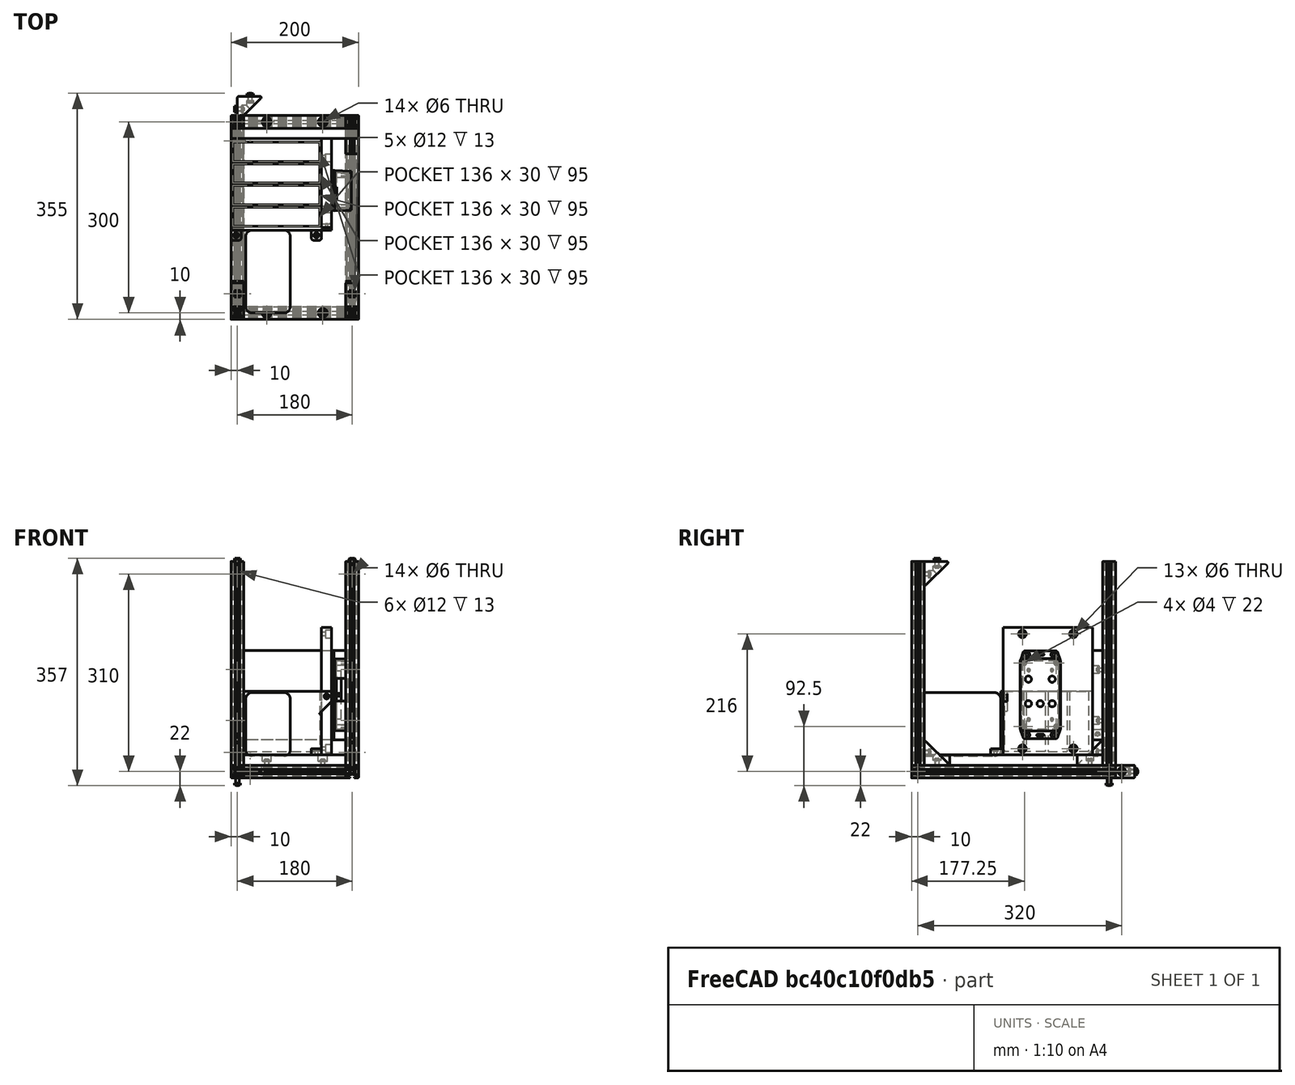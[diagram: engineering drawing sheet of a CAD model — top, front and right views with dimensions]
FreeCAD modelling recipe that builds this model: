
FCSTD DOCUMENT  (FreeCAD 0.17R9796 (Git))
Label: UPKframeNG2d
License: All rights reserved
LicenseURL: http://en.wikipedia.org/wiki/All_rights_reserved
objects: Part::Feature×60, Part::FeaturePython×24, Part::Compound×12, App::FeaturePython×8, App::Part×6, Part::Cylinder×5, Part::Box×4, Part::Cut×4, PartDesign::Body×2, PartDesign::Pocket×1, Part::Fillet×1, Part::MultiFuse×1
note: 115 computed .brp shape members not serialized (recipe doc carries the construction recipe); baked Part::Feature solids carry a one-line shape summary decoded from their .brp

FEATURE [Part::Feature] Pocket003001  label="tslot32con"
  Placement = pos=(0,10,10) rot=(1,0,0;1.5708rad)
  shape: bbox 20 x 320 x 20 mm, 150 faces (baked)
FEATURE [Part::Feature] Pocket003002  label="tslot16"
  Placement = pos=(10,0,10) rot=(0,1,0;1.5708rad)
  shape: bbox 160 x 20 x 20 mm, 94 faces (baked)
FEATURE [Part::Feature] Pocket003006  label="tslot16_001"
  Placement = pos=(10,-300,10) rot=(0,1,0;1.5708rad)
  shape: bbox 160 x 20 x 20 mm, 94 faces (baked)
FEATURE [Part::Feature] Pocket003007  label="tslot32con_001"
  Placement = pos=(180,-310,10) rot=(0,0.707107,0.707107;3.14159rad)
  shape: bbox 20 x 320 x 20 mm, 150 faces (baked)
FEATURE [Part::FeaturePython] Screw  label="M6x25-Screw"  # Fasteners workbench fastener (typed FeaturePython)
  Placement = pos=(-4,0,10) rot=(0,-1,0;1.5708rad)
  diameter = 7
  invert = false
  length = 6
  matchOuter = false
  offset = 0
  thread = false
  type = 15
FEATURE [Part::FeaturePython] Screw001  label="M6x25-Screw004"  # Fasteners workbench fastener (typed FeaturePython)
  Placement = pos=(-4,-300,10) rot=(0,-1,0;1.5708rad)
  diameter = 7
  invert = false
  length = 6
  matchOuter = false
  offset = 0
  thread = false
  type = 15
FEATURE [Part::FeaturePython] Screw002  label="M6x25-Screw005"  # Fasteners workbench fastener (typed FeaturePython)
  Placement = pos=(184,0,10) rot=(0,1,0;1.5708rad)
  diameter = 7
  invert = false
  length = 6
  matchOuter = false
  offset = 0
  thread = false
  type = 15
FEATURE [Part::FeaturePython] Screw004  label="M6x25-Screw006"  # Fasteners workbench fastener (typed FeaturePython)
  Placement = pos=(184,-300,10) rot=(0,1,0;1.5708rad)
  diameter = 7
  invert = false
  length = 6
  matchOuter = false
  offset = 0
  thread = false
  type = 15
FEATURE [App::Part] Part  label="lower_frame"
  Group = -> [Pocket003001,Pocket003002,Pocket003006,Pocket003007,Screw,Screw001,Screw002,Screw004]
  License = CC BY 3.0
  LicenseURL = http://creativecommons.org/licenses/by/3.0/
  Origin = -> PartOrigin
FEATURE [Part::Feature] Pocket003008  label="tslot32con001"
  Placement = pos=(0,10,10) rot=(1,0,0;1.5708rad)
  shape: bbox 20 x 320 x 20 mm, 150 faces (baked)
FEATURE [Part::Feature] Pocket003009  label="tslot041"
  Placement = pos=(10,0,10) rot=(0,1,0;1.5708rad)
  shape: bbox 160 x 20 x 20 mm, 94 faces (baked)
FEATURE [Part::Feature] Pocket003010  label="tslot16_002"
  Placement = pos=(10,-300,10) rot=(0,1,0;1.5708rad)
  shape: bbox 160 x 20 x 20 mm, 94 faces (baked)
FEATURE [Part::Feature] Pocket003011  label="tslot32con_002"
  Placement = pos=(180,-310,10) rot=(0,0.707107,0.707107;3.14159rad)
  shape: bbox 20 x 320 x 20 mm, 150 faces (baked)
FEATURE [Part::FeaturePython] Screw005  label="M6x25-Screw007"  # Fasteners workbench fastener (typed FeaturePython)
  Placement = pos=(-4,0,10) rot=(0,-1,0;1.5708rad)
  diameter = 7
  invert = false
  length = 6
  matchOuter = false
  offset = 0
  thread = false
  type = 15
FEATURE [Part::FeaturePython] Screw006  label="M6x25-Screw008"  # Fasteners workbench fastener (typed FeaturePython)
  Placement = pos=(-4,-300,10) rot=(0,-1,0;1.5708rad)
  diameter = 7
  invert = false
  length = 6
  matchOuter = false
  offset = 0
  thread = false
  type = 15
FEATURE [Part::FeaturePython] Screw007  label="M6x25-Screw009"  # Fasteners workbench fastener (typed FeaturePython)
  Placement = pos=(184,0,10) rot=(0,1,0;1.5708rad)
  diameter = 7
  invert = false
  length = 6
  matchOuter = false
  offset = 0
  thread = false
  type = 15
FEATURE [Part::FeaturePython] Screw008  label="M6x25-Screw010"  # Fasteners workbench fastener (typed FeaturePython)
  Placement = pos=(184,-300,10) rot=(0,1,0;1.5708rad)
  diameter = 7
  invert = false
  length = 6
  matchOuter = false
  offset = 0
  thread = false
  type = 15
FEATURE [App::Part] Part001  label="upper_frame"
  Group = -> [Pocket003008,Pocket003009,Pocket003010,Pocket003011,Screw005,Screw006,Screw007,Screw008]
  License = CC BY 3.0
  LicenseURL = http://creativecommons.org/licenses/by/3.0/
  Origin = -> PartOrigin001
  Placement = pos=(0,0,340) rot=(0,0,1;0rad)
FEATURE [Part::Feature] Fillet004001  label="Fillet005"
  shape: bbox 37.5 x 37.5 x 20 mm, 26 faces (baked)
FEATURE [Part::FeaturePython] Screw009  label="M6x12-Screw"  # Fasteners workbench fastener (typed FeaturePython)
  Placement = pos=(7,20,10) rot=(0,1,0;1.5708rad)
  diameter = 4
  invert = false
  length = 1
  matchOuter = false
  offset = 0
  thread = false
  type = 20
FEATURE [Part::Feature] Body001  label="m6nutplate"
  Placement = pos=(-1.5,15,5) rot=(0,-1,0;1.5708rad)
  shape: bbox 3 x 10 x 10 mm, 9 faces (baked)
FEATURE [App::Part] Part002  label="cornerstonescrewnut"
  License = CC BY 3.0
  LicenseURL = http://creativecommons.org/licenses/by/3.0/
  Origin = -> PartOrigin002
  Placement = pos=(10,-50,20) rot=(0,-1,0;1.5708rad)
FEATURE [Part::FeaturePython] Screw010  label="M6x12-Screw001"  # Fasteners workbench fastener (typed FeaturePython)
  Placement = pos=(20,33,10) rot=(1,0,0;1.5708rad)
  diameter = 4
  invert = false
  length = 1
  matchOuter = false
  offset = 0
  thread = false
  type = 20
FEATURE [Part::Feature] Body002  label="m6nutplate001"
  Placement = pos=(15,41.5,5) rot=(0.57735,0.57735,0.57735;4.18879rad)
  shape: bbox 10 x 3 x 10 mm, 9 faces (baked)
FEATURE [Part::Feature] Fillet004002  label="Fillet006"
  shape: bbox 37.5 x 37.5 x 20 mm, 26 faces (baked)
FEATURE [Part::FeaturePython] Screw011  label="M6x12-Screw002"  # Fasteners workbench fastener (typed FeaturePython)
  Placement = pos=(7,20,10) rot=(0,1,0;1.5708rad)
  diameter = 4
  invert = false
  length = 1
  matchOuter = false
  offset = 0
  thread = false
  type = 20
FEATURE [Part::Feature] Body003  label="m6nutplate002"
  Placement = pos=(-1.5,15,5) rot=(0,-1,0;1.5708rad)
  shape: bbox 3 x 10 x 10 mm, 9 faces (baked)
FEATURE [Part::FeaturePython] Screw012  label="M6x12-Screw003"  # Fasteners workbench fastener (typed FeaturePython)
  Placement = pos=(20,33,10) rot=(1,0,0;1.5708rad)
  diameter = 4
  invert = false
  length = 1
  matchOuter = false
  offset = 0
  thread = false
  type = 20
FEATURE [Part::Feature] Body004  label="m6nutplate003"
  Placement = pos=(15,41.5,5) rot=(0.57735,0.57735,0.57735;4.18879rad)
  shape: bbox 10 x 3 x 10 mm, 9 faces (baked)
FEATURE [App::Part] Part003  label="cornerstonescrewnut001"
  Group = -> [Body003,Screw011,Fillet004002,Screw012,Body004,PartOrigin002,Body001,Screw009,Fillet004001,Screw010,Body002,Part002]
  License = CC BY 3.0
  LicenseURL = http://creativecommons.org/licenses/by/3.0/
  Origin = -> PartOrigin003
  Placement = pos=(190,-50,20) rot=(0,-1,0;1.5708rad)
FEATURE [Part::Feature] Fillet004003  label="Fillet007"
  shape: bbox 37.5 x 37.5 x 20 mm, 26 faces (baked)
FEATURE [Part::FeaturePython] Screw013  label="M6x12-Screw004"  # Fasteners workbench fastener (typed FeaturePython)
  Placement = pos=(7,20,10) rot=(0,1,0;1.5708rad)
  diameter = 4
  invert = false
  length = 1
  matchOuter = false
  offset = 0
  thread = false
  type = 20
FEATURE [Part::Feature] Body005  label="m6nutplate004"
  Placement = pos=(-1.5,15,5) rot=(0,-1,0;1.5708rad)
  shape: bbox 3 x 10 x 10 mm, 9 faces (baked)
FEATURE [Part::FeaturePython] Screw014  label="M6x12-Screw005"  # Fasteners workbench fastener (typed FeaturePython)
  Placement = pos=(20,33,10) rot=(1,0,0;1.5708rad)
  diameter = 4
  invert = false
  length = 1
  matchOuter = false
  offset = 0
  thread = false
  type = 20
FEATURE [Part::Feature] Body006  label="m6nutplate005"
  Placement = pos=(15,41.5,5) rot=(0.57735,0.57735,0.57735;4.18879rad)
  shape: bbox 10 x 3 x 10 mm, 9 faces (baked)
FEATURE [App::Part] Part004  label="cornerstonescrewnut002"
  Group = -> [Body005,Screw013,Fillet004003,Screw014,Body006]
  License = CC BY 3.0
  LicenseURL = http://creativecommons.org/licenses/by/3.0/
  Origin = -> PartOrigin004
  Placement = pos=(-10,-50,340) rot=(0,1,0;1.5708rad)
FEATURE [Part::Feature] Fillet004004  label="Fillet008"
  shape: bbox 37.5 x 37.5 x 20 mm, 26 faces (baked)
FEATURE [Part::FeaturePython] Screw015  label="M6x12-Screw006"  # Fasteners workbench fastener (typed FeaturePython)
  Placement = pos=(7,20,10) rot=(0,1,0;1.5708rad)
  diameter = 4
  invert = false
  length = 1
  matchOuter = false
  offset = 0
  thread = false
  type = 20
FEATURE [Part::Feature] Body007  label="m6nutplate006"
  Placement = pos=(-1.5,15,5) rot=(0,-1,0;1.5708rad)
  shape: bbox 3 x 10 x 10 mm, 9 faces (baked)
FEATURE [Part::FeaturePython] Screw016  label="M6x12-Screw007"  # Fasteners workbench fastener (typed FeaturePython)
  Placement = pos=(20,33,10) rot=(1,0,0;1.5708rad)
  diameter = 4
  invert = false
  length = 1
  matchOuter = false
  offset = 0
  thread = false
  type = 20
FEATURE [Part::Feature] Body008  label="m6nutplate007"
  Placement = pos=(15,41.5,5) rot=(0.57735,0.57735,0.57735;4.18879rad)
  shape: bbox 10 x 3 x 10 mm, 9 faces (baked)
FEATURE [App::Part] Part005  label="cornerstonescrewnut003"
  Group = -> [Body007,Screw015,Fillet004004,Screw016,Body008]
  License = CC BY 3.0
  LicenseURL = http://creativecommons.org/licenses/by/3.0/
  Origin = -> PartOrigin005
  Placement = pos=(170,-50,340) rot=(0,1,0;1.5708rad)
FEATURE [Part::Feature] Body009001  label="m6nutplate010"
  Placement = pos=(-1.5,15,5) rot=(0,-1,0;1.5708rad)
  shape: bbox 3 x 10 x 10 mm, 9 faces (baked)
FEATURE [Part::Feature] Body010001  label="m6nutplate011"
  Placement = pos=(15,41.5,5) rot=(0.57735,0.57735,0.57735;4.18879rad)
  shape: bbox 10 x 3 x 10 mm, 9 faces (baked)
FEATURE [Part::Feature] Screw018001  label="M6x12-Screw010"
  Placement = pos=(20,33,10) rot=(1,0,0;1.5708rad)
  shape: bbox 10.5 x 15.3 x 10.5 mm, 15 faces (baked)
FEATURE [Part::Feature] Screw017001  label="M6x12-Screw011"
  Placement = pos=(7,20,10) rot=(0,1,0;1.5708rad)
  shape: bbox 15.3 x 10.5 x 10.5 mm, 15 faces (baked)
FEATURE [Part::Feature] Fillet004005001  label="Fillet010"
  shape: bbox 37.5 x 37.5 x 20 mm, 26 faces (baked)
FEATURE [Part::Compound] Compound
  Links = -> [Body009001,Fillet004005001,Screw017001,Body010001,Screw018001]
  Placement = pos=(10,-250,340) rot=(0.707107,0,-0.707107;3.14159rad)
FEATURE [Part::Feature] Body010002  label="m6nutplate012"
  Placement = pos=(-1.5,15,5) rot=(0,-1,0;1.5708rad)
  shape: bbox 3 x 10 x 10 mm, 9 faces (baked)
FEATURE [Part::Feature] Body010003  label="m6nutplate013"
  Placement = pos=(15,41.5,5) rot=(0.57735,0.57735,0.57735;4.18879rad)
  shape: bbox 10 x 3 x 10 mm, 9 faces (baked)
FEATURE [Part::Feature] Screw018002  label="M6x12-Screw012"
  Placement = pos=(20,33,10) rot=(1,0,0;1.5708rad)
  shape: bbox 10.5 x 15.3 x 10.5 mm, 15 faces (baked)
FEATURE [Part::Feature] Screw018003  label="M6x12-Screw013"
  Placement = pos=(7,20,10) rot=(0,1,0;1.5708rad)
  shape: bbox 15.3 x 10.5 x 10.5 mm, 15 faces (baked)
FEATURE [Part::Feature] Fillet004005002  label="Fillet011"
  shape: bbox 37.5 x 37.5 x 20 mm, 26 faces (baked)
FEATURE [Part::Compound] Compound001
  Links = -> [Body010002,Fillet004005002,Screw018003,Body010003,Screw018002]
  Placement = pos=(190,-250,340) rot=(0.707107,0,-0.707107;3.14159rad)
FEATURE [Part::Feature] Body010004  label="m6nutplate014"
  Placement = pos=(-1.5,15,5) rot=(0,-1,0;1.5708rad)
  shape: bbox 3 x 10 x 10 mm, 9 faces (baked)
FEATURE [Part::Feature] Body010005  label="m6nutplate015"
  Placement = pos=(15,41.5,5) rot=(0.57735,0.57735,0.57735;4.18879rad)
  shape: bbox 10 x 3 x 10 mm, 9 faces (baked)
FEATURE [Part::Feature] Screw018004  label="M6x12-Screw014"
  Placement = pos=(20,33,10) rot=(1,0,0;1.5708rad)
  shape: bbox 10.5 x 15.3 x 10.5 mm, 15 faces (baked)
FEATURE [Part::Feature] Screw018005  label="M6x12-Screw015"
  Placement = pos=(7,20,10) rot=(0,1,0;1.5708rad)
  shape: bbox 15.3 x 10.5 x 10.5 mm, 15 faces (baked)
FEATURE [Part::Feature] Fillet004005003  label="Fillet012"
  shape: bbox 37.5 x 37.5 x 20 mm, 26 faces (baked)
FEATURE [Part::Compound] Compound002
  Links = -> [Body010004,Fillet004005003,Screw018005,Body010005,Screw018004]
  Placement = pos=(10,-290,60) rot=(0.57735,0.57735,-0.57735;4.18879rad)
FEATURE [Part::Feature] Body010006  label="m6nutplate016"
  Placement = pos=(-1.5,15,5) rot=(0,-1,0;1.5708rad)
  shape: bbox 3 x 10 x 10 mm, 9 faces (baked)
FEATURE [Part::Feature] Body010007  label="m6nutplate017"
  Placement = pos=(15,41.5,5) rot=(0.57735,0.57735,0.57735;4.18879rad)
  shape: bbox 10 x 3 x 10 mm, 9 faces (baked)
FEATURE [Part::Feature] Screw018006  label="M6x12-Screw016"
  Placement = pos=(20,33,10) rot=(1,0,0;1.5708rad)
  shape: bbox 10.5 x 15.3 x 10.5 mm, 15 faces (baked)
FEATURE [Part::Feature] Screw018007  label="M6x12-Screw017"
  Placement = pos=(7,20,10) rot=(0,1,0;1.5708rad)
  shape: bbox 15.3 x 10.5 x 10.5 mm, 15 faces (baked)
FEATURE [Part::Feature] Fillet004005004  label="Fillet013"
  shape: bbox 37.5 x 37.5 x 20 mm, 26 faces (baked)
FEATURE [Part::Compound] Compound003
  Links = -> [Body010006,Fillet004005004,Screw018007,Body010007,Screw018006]
  Placement = pos=(190,-290,60) rot=(0.57735,0.57735,-0.57735;4.18879rad)
FEATURE [Part::Feature] Pocket001001  label="tslot32"
  Placement = pos=(0,0,20) rot=(0,0,1;0rad)
  shape: bbox 20 x 20 x 320 mm, 94 faces (baked)
FEATURE [Part::Feature] Body010008  label="m6nutplate018"
  Placement = pos=(-1.5,15,5) rot=(0,-1,0;1.5708rad)
  shape: bbox 3 x 10 x 10 mm, 9 faces (baked)
FEATURE [Part::Feature] Body010009  label="m6nutplate019"
  Placement = pos=(15,41.5,5) rot=(0.57735,0.57735,0.57735;4.18879rad)
  shape: bbox 10 x 3 x 10 mm, 9 faces (baked)
FEATURE [Part::Feature] Screw018008  label="M6x12-Screw018"
  Placement = pos=(20,33,10) rot=(1,0,0;1.5708rad)
  shape: bbox 10.5 x 15.3 x 10.5 mm, 15 faces (baked)
FEATURE [Part::Feature] Screw018009  label="M6x12-Screw019"
  Placement = pos=(7,20,10) rot=(0,1,0;1.5708rad)
  shape: bbox 15.3 x 10.5 x 10.5 mm, 15 faces (baked)
FEATURE [Part::Feature] Fillet004005005  label="Fillet014"
  shape: bbox 37.5 x 37.5 x 20 mm, 26 faces (baked)
FEATURE [Part::Compound] Compound004
  Links = -> [Body010008,Fillet004005005,Screw018009,Body010009,Screw018008]
  Placement = pos=(-10,-10,60) rot=(0.57735,-0.57735,0.57735;4.18879rad)
FEATURE [Part::Feature] Pocket003012  label="tslot32_001"
  Placement = pos=(0,-300,20) rot=(0,0,1;0rad)
  shape: bbox 20 x 20 x 320 mm, 94 faces (baked)
FEATURE [Part::Feature] Pocket003013  label="tslot32_002"
  Placement = pos=(180,0,20) rot=(0,0,1;0rad)
  shape: bbox 20 x 20 x 320 mm, 94 faces (baked)
FEATURE [Part::Feature] Pocket003014  label="tslot32_003"
  Placement = pos=(180,-300,20) rot=(0,0,1;0rad)
  shape: bbox 20 x 20 x 320 mm, 94 faces (baked)
FEATURE [PartDesign::Body] Body010027
FEATURE [Part::FeaturePython] Screw018021  label="M6x12-Screw032"  # Fasteners workbench fastener (typed FeaturePython)
  diameter = 4
  invert = false
  length = 1
  matchOuter = false
  offset = 0
  thread = false
  type = 20
FEATURE [Part::Feature] Body010028  label="m6nutplate032"
  Placement = pos=(5,-5,-8.39) rot=(0,1,0;3.14159rad)
  shape: bbox 10 x 10 x 3 mm, 9 faces (baked)
FEATURE [App::FeaturePython] circularEdgeConstraint009  # a2plus constraint (typed FeaturePython)
  Object1 = Screw
  Object2 = Body001
  SubElement1 = Edge7
  SubElement2 = Edge20
  Type = circularEdge
  directionConstraint = 1
  lockRotation = false
  offset = 0
FEATURE [Part::Compound] Compound017  label="nutplate12screw008"
  Links = -> [Screw018021,circularEdgeConstraint009,Body010028]
  Placement = pos=(10,30,6) rot=(0,0,1;0rad)
FEATURE [Part::FeaturePython] Screw018022  label="M6x12-Screw033"  # Fasteners workbench fastener (typed FeaturePython)
  diameter = 4
  invert = false
  length = 1
  matchOuter = false
  offset = 0
  thread = false
  type = 20
FEATURE [Part::Feature] Body010029  label="m6nutplate033"
  Placement = pos=(5,-5,-8.39) rot=(0,1,0;3.14159rad)
  shape: bbox 10 x 10 x 3 mm, 9 faces (baked)
FEATURE [App::FeaturePython] circularEdgeConstraint010  # a2plus constraint (typed FeaturePython)
  Object1 = Screw
  Object2 = Body001
  SubElement1 = Edge7
  SubElement2 = Edge20
  Type = circularEdge
  directionConstraint = 1
  lockRotation = false
  offset = 0
FEATURE [Part::Compound] Compound018  label="nutplate12screw009"
  Links = -> [Screw018022,circularEdgeConstraint010,Body010029]
  Placement = pos=(10,110,6) rot=(0,0,1;0rad)
FEATURE [Part::FeaturePython] Screw018023  label="M6x12-Screw034"  # Fasteners workbench fastener (typed FeaturePython)
  diameter = 4
  invert = false
  length = 1
  matchOuter = false
  offset = 0
  thread = false
  type = 20
FEATURE [Part::Feature] Body010030  label="m6nutplate034"
  Placement = pos=(5,-5,-8.39) rot=(0,1,0;3.14159rad)
  shape: bbox 10 x 10 x 3 mm, 9 faces (baked)
FEATURE [App::FeaturePython] circularEdgeConstraint011  # a2plus constraint (typed FeaturePython)
  Object1 = Screw
  Object2 = Body001
  SubElement1 = Edge7
  SubElement2 = Edge20
  Type = circularEdge
  directionConstraint = 1
  lockRotation = false
  offset = 0
FEATURE [Part::Compound] Compound019  label="nutplate12screw010"
  Links = -> [Screw018023,circularEdgeConstraint011,Body010030]
  Placement = pos=(190,110,6) rot=(0,0,1;0rad)
FEATURE [Part::FeaturePython] Screw018024  label="M6x12-Screw035"  # Fasteners workbench fastener (typed FeaturePython)
  diameter = 4
  invert = false
  length = 1
  matchOuter = false
  offset = 0
  thread = false
  type = 20
FEATURE [Part::Feature] Body010031  label="m6nutplate035"
  Placement = pos=(5,-5,-8.39) rot=(0,1,0;3.14159rad)
  shape: bbox 10 x 10 x 3 mm, 9 faces (baked)
FEATURE [App::FeaturePython] circularEdgeConstraint012  # a2plus constraint (typed FeaturePython)
  Object1 = Screw
  Object2 = Body001
  SubElement1 = Edge7
  SubElement2 = Edge20
  Type = circularEdge
  directionConstraint = 1
  lockRotation = false
  offset = 0
FEATURE [Part::Compound] Compound020  label="nutplate12screw011"
  Links = -> [Screw018024,circularEdgeConstraint012,Body010031]
  Placement = pos=(190,30,6) rot=(0,0,1;0rad)
FEATURE [Part::Compound] Compound021  label="front_plate"
  Links = -> [Body010027,Compound020,Compound019,Compound017,Compound018]
  Placement = pos=(-10,-10,60) rot=(1,0,0;1.5708rad)
FEATURE [Part::Compound] Compound016  label="bottom_plate"
  Placement = pos=(190,-310,20) rot=(0,0,1;1.5708rad)
FEATURE [PartDesign::Pocket] Pocket003019
  Length = 10
  Placement = pos=(130,-166,235) rot=(0,1,0;1.5708rad)
  Type = 0
FEATURE [Part::Box] Box003  label="MPPT"
  AttacherType = Attacher::AttachEngine3D
  Height = 100
  Length = 130
  Placement = pos=(290,128,10) rot=(0,0,1;0rad)
  Width = 70
FEATURE [Part::Fillet] Fillet007  label="MPPT               "
  Base = -> Box003
  Edges = 12 edges r=10: [Edge1,Edge2,Edge3,Edge4,Edge5,Edge6,Edge7,Edge8,Edge9,Edge10,Edge11,Edge12]
  Placement = pos=(211,-590,24) rot=(0,0,1;1.5708rad)
FEATURE [Part::Feature] Part__Feature1213  label="1591XXBF LID"
  Placement = pos=(153,-86,180) rot=(-0.57735,0.57735,0.57735;4.18879rad)
  shape: bbox 12.61 x 63.32 x 138 mm, 220 faces (baked)
FEATURE [Part::Feature] Part__Feature1212  label="1591XXB BOX"
  Placement = pos=(0,0,0) rot=(0,0.707107,0.707107;3.14159rad)
  shape: bbox 113.8 x 28.25 x 63.32 mm, 133 faces (baked)
FEATURE [Part::Cylinder] Cylinder  label="Zylinder"
  Angle = 360
  AttacherType = Attacher::AttachEngine3D
  Height = 60
  Placement = pos=(-14,48,18.6) rot=(1,0,0;1.5708rad)
  Radius = 5
FEATURE [Part::Cylinder] Cylinder001  label="Zylinder001"
  Angle = 360
  AttacherType = Attacher::AttachEngine3D
  Height = 60
  Placement = pos=(-14,48,0) rot=(1,0,0;1.5708rad)
  Radius = 5
FEATURE [Part::Cylinder] Cylinder002  label="Zylinder002"
  Angle = 360
  AttacherType = Attacher::AttachEngine3D
  Height = 60
  Placement = pos=(-14,48,-18.66) rot=(1,0,0;1.5708rad)
  Radius = 5
FEATURE [Part::Cylinder] Cylinder003  label="Zylinder003"
  Angle = 360
  AttacherType = Attacher::AttachEngine3D
  Height = 60
  Placement = pos=(24.49,48,18.6) rot=(1,0,0;1.5708rad)
  Radius = 5
FEATURE [Part::Cylinder] Cylinder004  label="Zylinder004"
  Angle = 360
  AttacherType = Attacher::AttachEngine3D
  Height = 60
  Placement = pos=(24.49,48,-18.66) rot=(1,0,0;1.5708rad)
  Radius = 5
FEATURE [Part::MultiFuse] Fusion
  Shapes = -> [Cylinder,Cylinder004,Cylinder003,Cylinder002,Cylinder001]
FEATURE [Part::Cut] Cut
  Base = -> Part__Feature1212
  Tool = -> Fusion
FEATURE [Part::Box] Box002  label="Würfel002"
  AttacherType = Attacher::AttachEngine3D
  Height = 10
  Length = 76
  Placement = pos=(-38,16,-36) rot=(0,0,1;0rad)
  Width = 12.6
FEATURE [Part::Cut] Cut001
  Base = -> Cut
  Tool = -> Box002
FEATURE [Part::Box] Box004  label="Würfel003"
  AttacherType = Attacher::AttachEngine3D
  Height = 10
  Length = 36
  Placement = pos=(-10,9,24) rot=(0,0,1;0rad)
  Width = 20
FEATURE [Part::Cut] Cut002
  Base = -> Cut001
  Tool = -> Box004
FEATURE [Part::Box] Box  label="Würfel"
  AttacherType = Attacher::AttachEngine3D
  Height = 20
  Length = 10
  Placement = pos=(49,23,-6) rot=(0,0,1;0rad)
  Width = 6
FEATURE [Part::Cut] Cut003  label="bms-cover"
  Base = -> Cut002
  Placement = pos=(179,-108,130.5) rot=(0.57735,-0.57735,0.57735;2.0944rad)
  Tool = -> Box
FEATURE [PartDesign::Body] Body010032
FEATURE [Part::FeaturePython] Screw018025  label="M6x12-Screw036"  # Fasteners workbench fastener (typed FeaturePython)
  diameter = 4
  invert = false
  length = 1
  matchOuter = false
  offset = 0
  thread = false
  type = 20
FEATURE [App::FeaturePython] circularEdgeConstraint013  # a2plus constraint (typed FeaturePython)
  Object1 = Screw
  Object2 = Body001
  SubElement1 = Edge7
  SubElement2 = Edge20
  Type = circularEdge
  directionConstraint = 1
  lockRotation = false
  offset = 0
FEATURE [Part::FeaturePython] Screw018026  label="M6x12-Screw037"  # Fasteners workbench fastener (typed FeaturePython)
  diameter = 4
  invert = false
  length = 1
  matchOuter = false
  offset = 0
  thread = false
  type = 20
FEATURE [Part::Feature] Body010034  label="m6nutplate037"
  Placement = pos=(5,-5,-8.39) rot=(0,1,0;3.14159rad)
  shape: bbox 10 x 10 x 3 mm, 9 faces (baked)
FEATURE [App::FeaturePython] circularEdgeConstraint014  # a2plus constraint (typed FeaturePython)
  Object1 = Screw
  Object2 = Body001
  SubElement1 = Edge7
  SubElement2 = Edge20
  Type = circularEdge
  directionConstraint = 1
  lockRotation = false
  offset = 0
FEATURE [Part::FeaturePython] Screw018027  label="M6x12-Screw038"  # Fasteners workbench fastener (typed FeaturePython)
  diameter = 4
  invert = false
  length = 1
  matchOuter = false
  offset = 0
  thread = false
  type = 20
FEATURE [Part::Feature] Body010035  label="m6nutplate038"
  Placement = pos=(5,-5,-8.39) rot=(0,1,0;3.14159rad)
  shape: bbox 10 x 10 x 3 mm, 9 faces (baked)
FEATURE [App::FeaturePython] circularEdgeConstraint015  # a2plus constraint (typed FeaturePython)
  Object1 = Screw
  Object2 = Body001
  SubElement1 = Edge7
  SubElement2 = Edge20
  Type = circularEdge
  directionConstraint = 1
  lockRotation = false
  offset = 0
FEATURE [Part::FeaturePython] Screw018028  label="M6x12-Screw039"  # Fasteners workbench fastener (typed FeaturePython)
  diameter = 4
  invert = false
  length = 1
  matchOuter = false
  offset = 0
  thread = false
  type = 20
FEATURE [Part::Feature] Body010036  label="m6nutplate039"
  Placement = pos=(5,-5,-8.39) rot=(0,1,0;3.14159rad)
  shape: bbox 10 x 10 x 3 mm, 9 faces (baked)
FEATURE [App::FeaturePython] circularEdgeConstraint016  # a2plus constraint (typed FeaturePython)
  Object1 = Screw
  Object2 = Body001
  SubElement1 = Edge7
  SubElement2 = Edge20
  Type = circularEdge
  directionConstraint = 1
  lockRotation = false
  offset = 0
FEATURE [Part::Compound] Compound026  label="bmsmounting_plate"
  Links = -> [Body010032]
  Placement = pos=(132,-26,36) rot=(0.707107,0,0.707107;3.14159rad)
FEATURE [Part::Feature] Body010037  label="batterymount"
  Placement = pos=(-10,-170,36) rot=(0,0,1;0rad)
  shape: bbox 158 x 176 x 100 mm, 72 faces (baked)
FEATURE [Part::Feature] Body010033  label="m6nutplate036"
  Placement = pos=(5,-5,-8.39) rot=(0,1,0;3.14159rad)
  shape: bbox 10 x 10 x 3 mm, 9 faces (baked)
